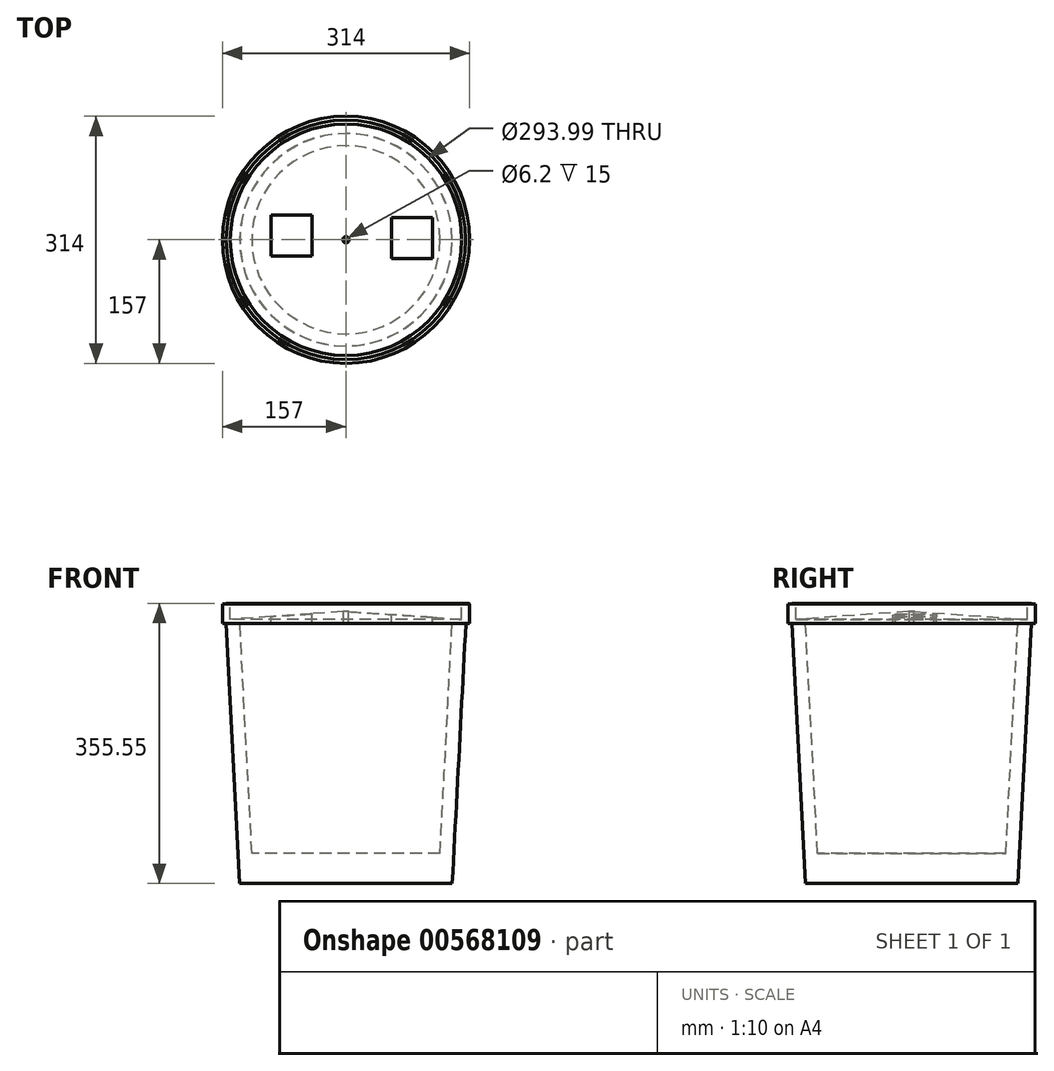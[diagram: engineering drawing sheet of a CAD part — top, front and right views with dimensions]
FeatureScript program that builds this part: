
annotation { "Feature Type Name" : "Feature", "Feature Type Description" : "" }
export const myFeature = defineFeature(function(context is Context, id is Id, definition is map)
    precondition{}
    {
        {
            var Q0;
            Q0=qCreatedBy(makeId("Top.planeOp"),FACE);
            var sketch = newSketch(context, id + "F0", { "sketchPlane" : qUnion([Q0])});
            skCircle(sketch, "E0", {"center": v(0, 0) * mm, "radius": 135 * mm});
            skSolve(sketch);
        }
        {
            var Q0;
            Q0=makeQuery(id+"F0.imprint","IMPRINT",FACE,{"disambiguationData":[TD([[makeQuery(id+"F0.imprint","IMPRINT",EDGE,{"derivedFrom":sQuery(id+"F0.wireOp",EDGE,"E0")}),1.0]])]});
            extrude(context, id + "F1", {"entities" : qUnion([Q0]), "depth" : 330.2 * mm, "offsetDistance" : 25 * mm, "hasDraft" : true, "draftAngle" : 3 * degree});
        }
        {
            var Q0;
            Q0=makeQuery(id+"F1.opExtrude","CAP_FACE",FACE,{"disambiguationData":[OSD([sQuery(id+"F0.wireOp",EDGE,"E0")])],"isStart":false});
            var sketch = newSketch(context, id + "F2", { "sketchPlane" : qUnion([Q0])});
            skCircle(sketch, "E1", {"center": v(0, 0) * mm, "radius": 134.8 * mm});
            skSolve(sketch);
        }
        {
            var Q0;
            Q0=makeQuery(id+"F2.imprint","IMPRINT",FACE,{"disambiguationData":[TD([[makeQuery(id+"F2.imprint","IMPRINT",EDGE,{"derivedFrom":sQuery(id+"F2.wireOp",EDGE,"E1")}),1.0]])]});
            extrude(context, id + "F3", {"entities" : qUnion([Q0]), "operationType" : NewBodyOperationType.REMOVE, "oppositeDirection" : true, "depth" : 292.1 * mm, "offsetDistance" : 25 * mm, "hasDraft" : true, "draftAngle" : 3 * degree, "draftPullDirection" : true});
        }
        {
            var Q0;
            Q0=makeQuery(id+"F1.opExtrude","CAP_FACE",FACE,{"disambiguationData":[OSD([sQuery(id+"F0.wireOp",EDGE,"E0")])],"isStart":false});
            var sketch = newSketch(context, id + "F4", { "sketchPlane" : qUnion([Q0])});
            skCircle(sketch, "E2", {"center": v(0, 0) * mm, "radius": 157 * mm});
            skSolve(sketch);
        }
        {
            var Q0;
            Q0 = qSketchRegion(id + "F4", true);
            extrude(context, id + "F5", {"entities" : qUnion([Q0]), "operationType" : NewBodyOperationType.ADD, "depth" : 25 * mm, "offsetDistance" : 25 * mm});
        }
        {
            var Q0;
            Q0=makeQuery(id+"F5.opExtrude","CAP_FACE",FACE,{"disambiguationData":[OSD([sQuery(id+"F4.wireOp",EDGE,"E2")])],"isStart":false});
            var sketch = newSketch(context, id + "F6", { "sketchPlane" : qUnion([Q0])});
            skCircle(sketch, "E3.0", {"center": v(0, 0) * mm, "radius": 147 * mm});
            skLineSegment(sketch, "E4.bottom", {"start": v(-95.16, 31.59) * mm, "end": v(-43.16, 31.59) * mm});
            skLineSegment(sketch, "E4.top", {"start": v(-95.16, -20.41) * mm, "end": v(-43.16, -20.41) * mm});
            skLineSegment(sketch, "E4.left", {"start": v(-95.16, 31.59) * mm, "end": v(-95.16, -20.41) * mm});
            skLineSegment(sketch, "E4.right", {"start": v(-43.16, 31.59) * mm, "end": v(-43.16, -20.41) * mm});
            skLineSegment(sketch, "E5.bottom", {"start": v(57.91, 28.2) * mm, "end": v(109.91, 28.2) * mm});
            skLineSegment(sketch, "E5.top", {"start": v(57.91, -23.8) * mm, "end": v(109.91, -23.8) * mm});
            skLineSegment(sketch, "E5.left", {"start": v(57.91, 28.2) * mm, "end": v(57.91, -23.8) * mm});
            skLineSegment(sketch, "E5.right", {"start": v(109.91, 28.2) * mm, "end": v(109.91, -23.8) * mm});
            skCircle(sketch, "E6", {"center": v(0, 0) * mm, "radius": 3.1 * mm});
            skSolve(sketch);
        }
        {
            var Q0;
            Q0=makeQuery(id+"F6.imprint","IMPRINT",FACE,{"disambiguationData":[TD([[makeQuery(id+"F6.imprint","IMPRINT",EDGE,{"derivedFrom":sQuery(id+"F6.wireOp",EDGE,"E3.0")}),1.0]])]});
            var Q1;
            Q1=makeQuery(id+"F6.imprint","IMPRINT",FACE,{"disambiguationData":[TD([[makeQuery(id+"F6.imprint","IMPRINT",EDGE,{"derivedFrom":sQuery(id+"F6.wireOp",EDGE,"E5.bottom")}),-1.0]])]});
            var Q2;
            Q2=makeQuery(id+"F6.imprint","IMPRINT",FACE,{"disambiguationData":[TD([[makeQuery(id+"F6.imprint","IMPRINT",EDGE,{"derivedFrom":sQuery(id+"F6.wireOp",EDGE,"E4.bottom")}),-1.0]])]});
            var Q3;
            Q3=makeQuery(id+"F6.imprint","IMPRINT",FACE,{"disambiguationData":[TD([[makeQuery(id+"F6.imprint","IMPRINT",EDGE,{"derivedFrom":sQuery(id+"F6.wireOp",EDGE,"E6")}),1.0]])]});
            extrude(context, id + "F7", {"entities" : qUnion([Q0, Q1, Q2, Q3]), "operationType" : NewBodyOperationType.REMOVE, "oppositeDirection" : true, "depth" : 20 * mm, "offsetDistance" : 25 * mm});
        }
        {
            var Q0;
            Q0=makeQuery(id+"F7.boolean.opBoolean","COPY",FACE,{"derivedFrom":makeQuery(id+"F7.opExtrude","CAP_FACE",FACE,{"disambiguationData":[OSD([sQuery(id+"F6.wireOp",EDGE,"E3.0")])],"isStart":false})});
            var Q1;
            Q1=makeQuery(id+"F7.boolean.opBoolean","SPLIT",FACE,{"disambiguationData":[TD([makeQuery(id+"F7.opExtrude","SWEPT_FACE",FACE,{"disambiguationData":[OSD([sQuery(id+"F6.wireOp",EDGE,"E4.bottom")])]})])],"derivedFrom":makeQuery(id+"F5.opExtrude","CAP_FACE",FACE,{"disambiguationData":[OSD([sQuery(id+"F4.wireOp",EDGE,"E2")])],"isStart":false})});
            var Q2;
            Q2=makeQuery(id+"F7.boolean.opBoolean","SPLIT",FACE,{"disambiguationData":[TD([makeQuery(id+"F7.opExtrude","SWEPT_FACE",FACE,{"disambiguationData":[OSD([sQuery(id+"F6.wireOp",EDGE,"E6")])]})])],"derivedFrom":makeQuery(id+"F5.opExtrude","CAP_FACE",FACE,{"disambiguationData":[OSD([sQuery(id+"F4.wireOp",EDGE,"E2")])],"isStart":false})});
            var Q3;
            Q3=makeQuery(id+"F7.boolean.opBoolean","SPLIT",FACE,{"disambiguationData":[TD([makeQuery(id+"F7.opExtrude","SWEPT_FACE",FACE,{"disambiguationData":[OSD([sQuery(id+"F6.wireOp",EDGE,"E5.bottom")])]})])],"derivedFrom":makeQuery(id+"F5.opExtrude","CAP_FACE",FACE,{"disambiguationData":[OSD([sQuery(id+"F4.wireOp",EDGE,"E2")])],"isStart":false})});
            extrude(context, id + "F8", {"entities" : qUnion([Q0, Q1, Q2, Q3]), "operationType" : NewBodyOperationType.ADD, "depth" : 10 * mm, "offsetDistance" : 25 * mm, "hasDraft" : true, "draftAngle" : 86 * degree, "draftPullDirection" : true});
        }
        {
            var Q0;
            Q0=makeQuery(id+"F6.imprint","IMPRINT",FACE,{"disambiguationData":[TD([[makeQuery(id+"F6.imprint","IMPRINT",EDGE,{"derivedFrom":sQuery(id+"F6.wireOp",EDGE,"E5.bottom")}),-1.0]])]});
            var Q1;
            Q1=makeQuery(id+"F6.imprint","IMPRINT",FACE,{"disambiguationData":[TD([[makeQuery(id+"F6.imprint","IMPRINT",EDGE,{"derivedFrom":sQuery(id+"F6.wireOp",EDGE,"E4.bottom")}),-1.0]])]});
            var Q2;
            Q2=makeQuery(id+"F6.imprint","IMPRINT",FACE,{"disambiguationData":[TD([[makeQuery(id+"F6.imprint","IMPRINT",EDGE,{"derivedFrom":sQuery(id+"F6.wireOp",EDGE,"E6")}),1.0]])]});
            extrude(context, id + "F9", {"entities" : qUnion([Q0, Q1, Q2]), "operationType" : NewBodyOperationType.REMOVE, "oppositeDirection" : true, "depth" : 254 * mm, "offsetDistance" : 25 * mm});
        }
    });
